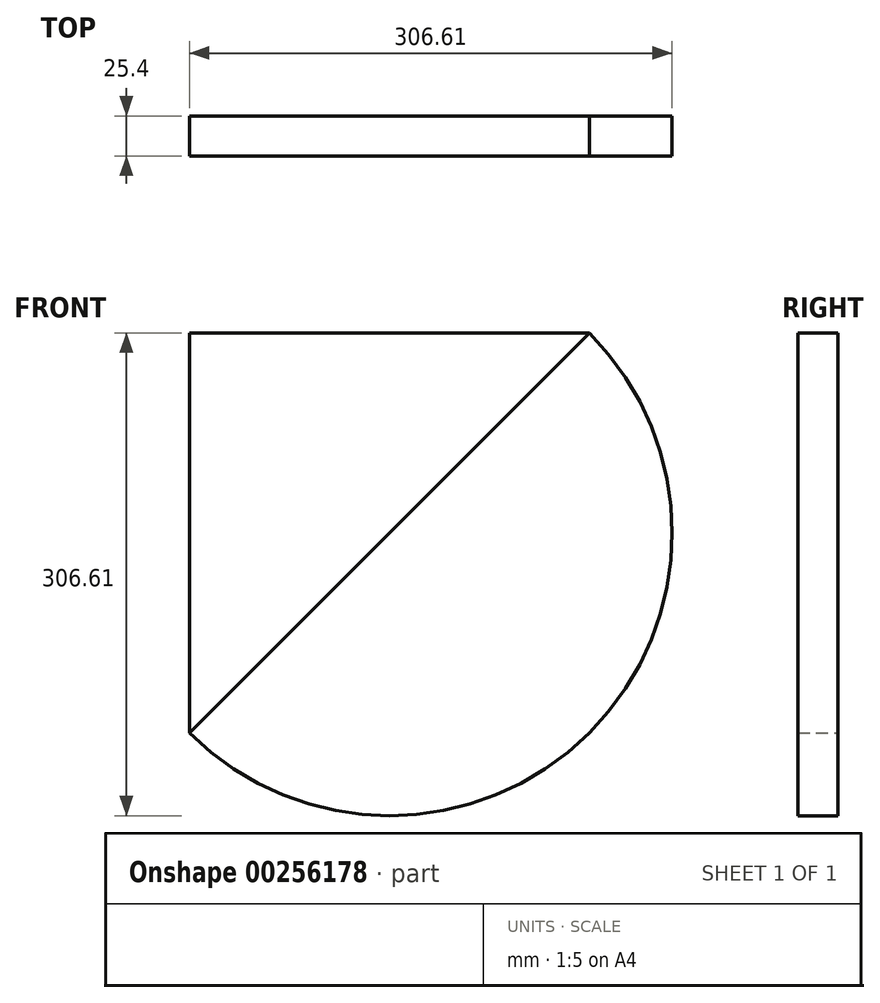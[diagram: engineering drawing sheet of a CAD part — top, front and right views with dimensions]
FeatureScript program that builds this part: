
annotation { "Feature Type Name" : "Feature", "Feature Type Description" : "" }
export const myFeature = defineFeature(function(context is Context, id is Id, definition is map)
    precondition{}
    {
        {
            var Q0;
            Q0=qCreatedBy(makeId("Front.planeOp"),FACE);
            var sketch = newSketch(context, id + "F0", { "sketchPlane" : qUnion([Q0])});
            skLineSegment(sketch, "E0.bottom", {"start": v(-127, 127) * mm, "end": v(127, 127) * mm});
            skLineSegment(sketch, "E0.left", {"start": v(-127, 127) * mm, "end": v(-127, -127) * mm});
            skPoint(sketch, "E0.middle", {"position": v(0, 0) * mm});
            skLineSegment(sketch, "E1", {"start": v(-127, -127) * mm, "end": v(127, 127) * mm});
            skArc(sketch, "E2", {"start": v(-127, -127) * mm, "mid": v(127, -127) * mm, "end": v(127, 127) * mm});
            skSolve(sketch);
        }
        {
            var Q0;
            Q0=makeQuery(id+"F0.imprint","IMPRINT",FACE,{"disambiguationData":[TD([[makeQuery(id+"F0.imprint","IMPRINT",EDGE,{"derivedFrom":sQuery(id+"F0.wireOp",EDGE,"E0.bottom")}),-1.0]])]});
            extrude(context, id + "F1", {"entities" : qUnion([Q0]), "depth" : 25.4 * mm});
        }
        {
            var Q0;
            Q0 = qSketchRegion(id + "F0", true);
            extrude(context, id + "F2", {"entities" : qUnion([Q0]), "depth" : 25.4 * mm});
        }
        {
            var Q0;
            Q0=makeQuery(id+"F1.opExtrude","SWEPT_BODY",BODY,{"disambiguationData":[OSD([sQuery(id+"F0.wireOp",EDGE,"E0.bottom"),sQuery(id+"F0.wireOp",EDGE,"E0.left"),sQuery(id+"F0.wireOp",EDGE,"E1")])]});
            var Q1;
            Q1=makeQuery(id+"F2.opExtrude","SWEPT_BODY",BODY,{"disambiguationData":[OSD([sQuery(id+"F0.wireOp",EDGE,"E0.bottom"),sQuery(id+"F0.wireOp",EDGE,"E0.left"),sQuery(id+"F0.wireOp",EDGE,"E2")])]});
            booleanBodies(context, id + "F3", {"operationType" : BooleanOperationType.SUBTRACTION, "tools" : qUnion([Q0]), "targets" : qUnion([Q1]), "keepTools" : true});
        }
    });
